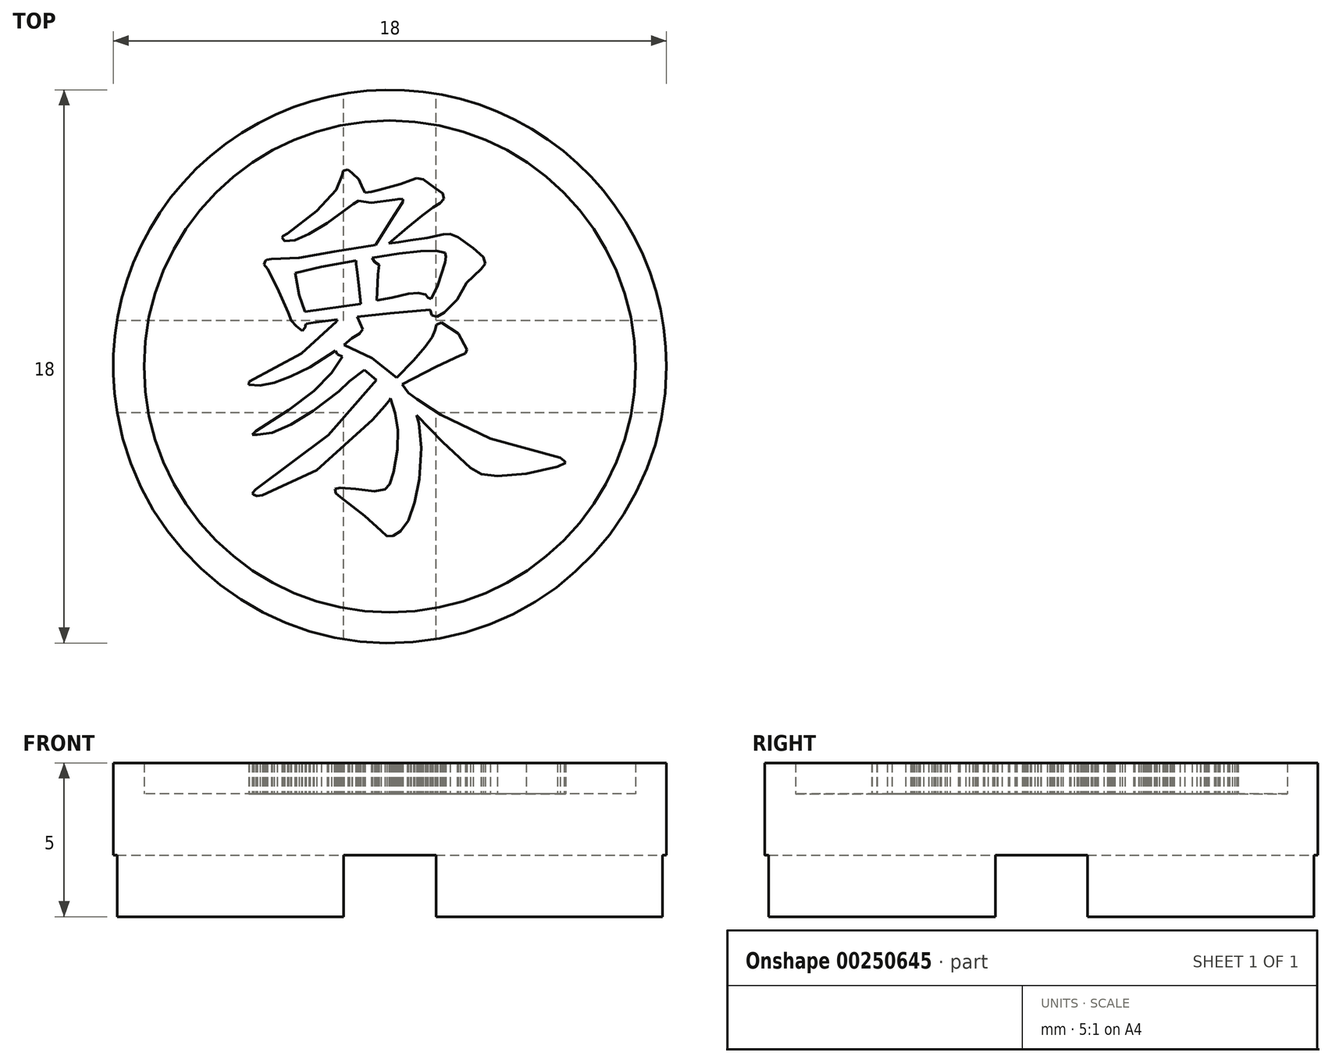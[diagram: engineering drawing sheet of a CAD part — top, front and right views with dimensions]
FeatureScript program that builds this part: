
annotation { "Feature Type Name" : "Feature", "Feature Type Description" : "" }
export const myFeature = defineFeature(function(context is Context, id is Id, definition is map)
    precondition{}
    {
        {
            var Q0;
            Q0=qCreatedBy(makeId("Top.planeOp"),FACE);
            var sketch = newSketch(context, id + "F0", { "sketchPlane" : qUnion([Q0])});
            skCircle(sketch, "E0", {"center": v(-31.33, 19.76) * mm, "radius": 9 * mm});
            skSolve(sketch);
        }
        {
            var Q0;
            Q0=qSketchRegion(id+"F0",true);
            extrude(context, id + "F1", {"entities" : qUnion([Q0]), "depth" : 4 * mm});
        }
        {
            var Q0;
            Q0=makeQuery(id+"F1.opExtrude","CAP_FACE",FACE,{"disambiguationData":[OSD([sQuery(id+"F0.wireOp",EDGE,"E0")])],"isStart":false});
            var sketch = newSketch(context, id + "F2", { "sketchPlane" : qUnion([Q0])});
            skCircle(sketch, "E1", {"center": v(-31.33, 19.76) * mm, "radius": 8 * mm});
            skCircle(sketch, "E2", {"center": v(-31.33, 19.76) * mm, "radius": 9 * mm});
            skSolve(sketch);
        }
        {
            var Q0;
            Q0=makeQuery(id+"F1.opExtrude","CAP_FACE",FACE,{"disambiguationData":[OSD([sQuery(id+"F0.wireOp",EDGE,"E0")])],"isStart":true});
            var sketch = newSketch(context, id + "F3", { "sketchPlane" : qUnion([Q0])});
            skLineSegment(sketch, "E3", {"start": v(-31.33, -19.76) * mm, "end": v(-22.33, -19.76) * mm, "construction": true});
            skLineSegment(sketch, "E4", {"start": v(-31.33, -19.76) * mm, "end": v(-31.33, -10.76) * mm, "construction": true});
            skLineSegment(sketch, "E5", {"start": v(-31.33, -19.76) * mm, "end": v(-40.33, -19.76) * mm, "construction": true});
            skLineSegment(sketch, "E6", {"start": v(-31.33, -19.76) * mm, "end": v(-31.33, -28.76) * mm, "construction": true});
            skLineSegment(sketch, "E7.bottom", {"start": v(-40.33, -28.76) * mm, "end": v(-22.33, -28.76) * mm});
            skLineSegment(sketch, "E7.top", {"start": v(-40.33, -10.76) * mm, "end": v(-22.33, -10.76) * mm});
            skLineSegment(sketch, "E7.left", {"start": v(-22.33, -10.76) * mm, "end": v(-22.33, -28.76) * mm});
            skLineSegment(sketch, "E7.right", {"start": v(-40.33, -10.76) * mm, "end": v(-40.33, -28.76) * mm});
            skPoint(sketch, "E8", {"position": v(-31.33, -28.76) * mm});
            skPoint(sketch, "E9", {"position": v(-40.33, -19.76) * mm});
            skPoint(sketch, "E10", {"position": v(-22.33, -19.76) * mm});
            skPoint(sketch, "E11", {"position": v(-31.33, -10.76) * mm});
            skLineSegment(sketch, "E12.bottom", {"start": v(-32.83, -10.76) * mm, "end": v(-29.83, -10.76) * mm});
            skLineSegment(sketch, "E12.top", {"start": v(-32.83, -28.76) * mm, "end": v(-29.83, -28.76) * mm});
            skLineSegment(sketch, "E12.left", {"start": v(-32.83, -10.76) * mm, "end": v(-32.83, -28.76) * mm});
            skLineSegment(sketch, "E12.right", {"start": v(-29.83, -10.76) * mm, "end": v(-29.83, -28.76) * mm});
            skLineSegment(sketch, "E13.bottom", {"start": v(-40.33, -18.26) * mm, "end": v(-22.33, -18.26) * mm});
            skLineSegment(sketch, "E13.top", {"start": v(-40.33, -21.26) * mm, "end": v(-22.33, -21.26) * mm});
            skLineSegment(sketch, "E13.left", {"start": v(-40.33, -18.26) * mm, "end": v(-40.33, -21.26) * mm});
            skLineSegment(sketch, "E13.right", {"start": v(-22.33, -18.26) * mm, "end": v(-22.33, -21.26) * mm});
            skSolve(sketch);
        }
        {
            var Q0;
            {var subQ1=sQuery(id+"F3.wireOp",EDGE,"E12.bottom");var subQ3=makeQuery(id+"F1.opExtrude","CAP_EDGE",EDGE,{"disambiguationData":[OSD([sQuery(id+"F0.wireOp",EDGE,"E0")])],"isStart":true});var subQ4=makeQuery(id+"F3.imprint","INTERSECT",VERTEX,{"derivedFrom":[subQ3,subQ1]});Q0=makeQuery(id+"F3.imprint","IMPRINT",FACE,{"disambiguationData":[TD([[makeQuery(id+"F3.imprint","IMPRINT",EDGE,{"disambiguationData":[TD([[subQ4,1.0]])],"derivedFrom":subQ3}),1.0]])]});}
            var Q1;
            {var subQ1=sQuery(id+"F3.wireOp",EDGE,"E12.bottom");var subQ3=makeQuery(id+"F1.opExtrude","CAP_EDGE",EDGE,{"disambiguationData":[OSD([sQuery(id+"F0.wireOp",EDGE,"E0")])],"isStart":true});var subQ4=makeQuery(id+"F3.imprint","INTERSECT",VERTEX,{"derivedFrom":[subQ3,subQ1]});Q1=makeQuery(id+"F3.imprint","IMPRINT",FACE,{"disambiguationData":[TD([[makeQuery(id+"F3.imprint","IMPRINT",EDGE,{"disambiguationData":[TD([[subQ4,-1.0]])],"derivedFrom":subQ3}),1.0]])]});}
            var Q2;
            {var subQ1=sQuery(id+"F3.wireOp",EDGE,"E12.top");var subQ3=makeQuery(id+"F1.opExtrude","CAP_EDGE",EDGE,{"disambiguationData":[OSD([sQuery(id+"F0.wireOp",EDGE,"E0")])],"isStart":true});var subQ4=makeQuery(id+"F3.imprint","INTERSECT",VERTEX,{"derivedFrom":[subQ3,subQ1]});Q2=makeQuery(id+"F3.imprint","IMPRINT",FACE,{"disambiguationData":[TD([[makeQuery(id+"F3.imprint","IMPRINT",EDGE,{"disambiguationData":[TD([[subQ4,-1.0]])],"derivedFrom":subQ3}),1.0]])]});}
            var Q3;
            {var subQ1=sQuery(id+"F3.wireOp",EDGE,"E12.top");var subQ3=makeQuery(id+"F1.opExtrude","CAP_EDGE",EDGE,{"disambiguationData":[OSD([sQuery(id+"F0.wireOp",EDGE,"E0")])],"isStart":true});var subQ4=makeQuery(id+"F3.imprint","INTERSECT",VERTEX,{"derivedFrom":[subQ3,subQ1]});Q3=makeQuery(id+"F3.imprint","IMPRINT",FACE,{"disambiguationData":[TD([[makeQuery(id+"F3.imprint","IMPRINT",EDGE,{"disambiguationData":[TD([[subQ4,1.0]])],"derivedFrom":subQ3}),1.0]])]});}
            var Q4;
            {var subQ0=sQuery(id+"F3.wireOp",EDGE,"E13.left");var subQ3=makeQuery(id+"F1.opExtrude","CAP_EDGE",EDGE,{"disambiguationData":[OSD([sQuery(id+"F0.wireOp",EDGE,"E0")])],"isStart":true});var subQ5=makeQuery(id+"F3.imprint","INTERSECT",VERTEX,{"derivedFrom":[subQ3,subQ0]});Q4=makeQuery(id+"F3.imprint","IMPRINT",FACE,{"disambiguationData":[TD([[makeQuery(id+"F3.imprint","IMPRINT",EDGE,{"disambiguationData":[TD([[subQ5,-1.0]])],"derivedFrom":subQ3}),1.0]])]});}
            var Q5;
            {var subQ0=sQuery(id+"F3.wireOp",EDGE,"E13.right");var subQ3=makeQuery(id+"F1.opExtrude","CAP_EDGE",EDGE,{"disambiguationData":[OSD([sQuery(id+"F0.wireOp",EDGE,"E0")])],"isStart":true});var subQ5=makeQuery(id+"F3.imprint","INTERSECT",VERTEX,{"derivedFrom":[subQ3,subQ0]});Q5=makeQuery(id+"F3.imprint","IMPRINT",FACE,{"disambiguationData":[TD([[makeQuery(id+"F3.imprint","IMPRINT",EDGE,{"disambiguationData":[TD([[subQ5,1.0]])],"derivedFrom":subQ3}),1.0]])]});}
            var Q6;
            {var subQ0=sQuery(id+"F3.wireOp",EDGE,"E13.left");var subQ3=makeQuery(id+"F1.opExtrude","CAP_EDGE",EDGE,{"disambiguationData":[OSD([sQuery(id+"F0.wireOp",EDGE,"E0")])],"isStart":true});var subQ5=makeQuery(id+"F3.imprint","INTERSECT",VERTEX,{"derivedFrom":[subQ3,subQ0]});Q6=makeQuery(id+"F3.imprint","IMPRINT",FACE,{"disambiguationData":[TD([[makeQuery(id+"F3.imprint","IMPRINT",EDGE,{"disambiguationData":[TD([[subQ5,1.0]])],"derivedFrom":subQ3}),1.0]])]});}
            var Q7;
            {var subQ0=sQuery(id+"F3.wireOp",EDGE,"E13.right");var subQ3=makeQuery(id+"F1.opExtrude","CAP_EDGE",EDGE,{"disambiguationData":[OSD([sQuery(id+"F0.wireOp",EDGE,"E0")])],"isStart":true});var subQ5=makeQuery(id+"F3.imprint","INTERSECT",VERTEX,{"derivedFrom":[subQ3,subQ0]});Q7=makeQuery(id+"F3.imprint","IMPRINT",FACE,{"disambiguationData":[TD([[makeQuery(id+"F3.imprint","IMPRINT",EDGE,{"disambiguationData":[TD([[subQ5,-1.0]])],"derivedFrom":subQ3}),1.0]])]});}
            var Q8;
            {var subQ3=makeQuery(id+"F1.opExtrude","CAP_EDGE",EDGE,{"disambiguationData":[OSD([sQuery(id+"F0.wireOp",EDGE,"E0")])],"isStart":true});var subQ5=sQuery(id+"F3.wireOp",EDGE,"E12.left");var subQ8=makeQuery(id+"F3.imprint","INTERSECT",VERTEX,{"disambiguationData":[OD(1.0)],"derivedFrom":[subQ3,subQ5]});Q8=makeQuery(id+"F3.imprint","IMPRINT",FACE,{"disambiguationData":[TD([[makeQuery(id+"F3.imprint","IMPRINT",EDGE,{"disambiguationData":[TD([[subQ8,-1.0]])],"derivedFrom":subQ3}),1.0]])]});}
            var Q9;
            {var subQ3=makeQuery(id+"F1.opExtrude","CAP_EDGE",EDGE,{"disambiguationData":[OSD([sQuery(id+"F0.wireOp",EDGE,"E0")])],"isStart":true});var subQ5=sQuery(id+"F3.wireOp",EDGE,"E12.right");var subQ8=makeQuery(id+"F3.imprint","INTERSECT",VERTEX,{"disambiguationData":[OD(1.0)],"derivedFrom":[subQ3,subQ5]});Q9=makeQuery(id+"F3.imprint","IMPRINT",FACE,{"disambiguationData":[TD([[makeQuery(id+"F3.imprint","IMPRINT",EDGE,{"disambiguationData":[TD([[subQ8,1.0]])],"derivedFrom":subQ3}),1.0]])]});}
            var Q10;
            {var subQ3=makeQuery(id+"F1.opExtrude","CAP_EDGE",EDGE,{"disambiguationData":[OSD([sQuery(id+"F0.wireOp",EDGE,"E0")])],"isStart":true});var subQ5=sQuery(id+"F3.wireOp",EDGE,"E12.left");var subQ8=makeQuery(id+"F3.imprint","INTERSECT",VERTEX,{"disambiguationData":[OD(0.0)],"derivedFrom":[subQ3,subQ5]});Q10=makeQuery(id+"F3.imprint","IMPRINT",FACE,{"disambiguationData":[TD([[makeQuery(id+"F3.imprint","IMPRINT",EDGE,{"disambiguationData":[TD([[subQ8,1.0]])],"derivedFrom":subQ3}),1.0]])]});}
            var Q11;
            {var subQ3=makeQuery(id+"F1.opExtrude","CAP_EDGE",EDGE,{"disambiguationData":[OSD([sQuery(id+"F0.wireOp",EDGE,"E0")])],"isStart":true});var subQ5=sQuery(id+"F3.wireOp",EDGE,"E12.right");var subQ8=makeQuery(id+"F3.imprint","INTERSECT",VERTEX,{"disambiguationData":[OD(0.0)],"derivedFrom":[subQ3,subQ5]});Q11=makeQuery(id+"F3.imprint","IMPRINT",FACE,{"disambiguationData":[TD([[makeQuery(id+"F3.imprint","IMPRINT",EDGE,{"disambiguationData":[TD([[subQ8,-1.0]])],"derivedFrom":subQ3}),1.0]])]});}
            var Q12;
            {var subQ2=sQuery(id+"F3.wireOp",EDGE,"E12.left");var subQ4=sQuery(id+"F3.wireOp",EDGE,"E13.bottom");var subQ8=makeQuery(id+"F3.imprint","INTERSECT",VERTEX,{"derivedFrom":[subQ2,subQ4]});Q12=makeQuery(id+"F3.imprint","IMPRINT",FACE,{"disambiguationData":[TD([[makeQuery(id+"F3.imprint","IMPRINT",EDGE,{"disambiguationData":[TD([[subQ8,1.0]])],"derivedFrom":subQ2}),1.0]])]});}
            var Q13;
            {var subQ1=sQuery(id+"F3.wireOp",EDGE,"E12.left");var subQ5=sQuery(id+"F3.wireOp",EDGE,"E13.bottom");var subQ6=makeQuery(id+"F3.imprint","INTERSECT",VERTEX,{"derivedFrom":[subQ1,subQ5]});Q13=makeQuery(id+"F3.imprint","IMPRINT",FACE,{"disambiguationData":[TD([[makeQuery(id+"F3.imprint","IMPRINT",EDGE,{"disambiguationData":[TD([[subQ6,-1.0]])],"derivedFrom":subQ1}),-1.0]])]});}
            var Q14;
            {var subQ0=sQuery(id+"F3.wireOp",EDGE,"E13.top");var subQ1=sQuery(id+"F3.wireOp",EDGE,"E12.left");var subQ2=makeQuery(id+"F3.imprint","INTERSECT",VERTEX,{"derivedFrom":[subQ1,subQ0]});Q14=makeQuery(id+"F3.imprint","IMPRINT",FACE,{"disambiguationData":[TD([[makeQuery(id+"F3.imprint","IMPRINT",EDGE,{"disambiguationData":[TD([[subQ2,-1.0]])],"derivedFrom":subQ1}),1.0]])]});}
            var Q15;
            {var subQ2=sQuery(id+"F3.wireOp",EDGE,"E13.bottom");var subQ5=sQuery(id+"F3.wireOp",EDGE,"E12.right");var subQ8=makeQuery(id+"F3.imprint","INTERSECT",VERTEX,{"derivedFrom":[subQ5,subQ2]});Q15=makeQuery(id+"F3.imprint","IMPRINT",FACE,{"disambiguationData":[TD([[makeQuery(id+"F3.imprint","IMPRINT",EDGE,{"disambiguationData":[TD([[subQ8,-1.0]])],"derivedFrom":subQ5}),1.0]])]});}
            var Q16;
            {var subQ0=sQuery(id+"F3.wireOp",EDGE,"E13.bottom");var subQ1=sQuery(id+"F3.wireOp",EDGE,"E12.left");var subQ2=makeQuery(id+"F3.imprint","INTERSECT",VERTEX,{"derivedFrom":[subQ1,subQ0]});Q16=makeQuery(id+"F3.imprint","IMPRINT",FACE,{"disambiguationData":[TD([[makeQuery(id+"F3.imprint","IMPRINT",EDGE,{"disambiguationData":[TD([[subQ2,-1.0]])],"derivedFrom":subQ1}),1.0]])]});}
            extrude(context, id + "F4", {"entities" : qUnion([Q0, Q1, Q2, Q3, Q4, Q5, Q6, Q7, Q8, Q9, Q10, Q11, Q12, Q13, Q14, Q15, Q16]), "operationType" : NewBodyOperationType.REMOVE, "oppositeDirection" : true, "depth" : 2 * mm});
        }
        {
            var Q0;
            Q0=qSketchRegion(id+"F2",true);
            var Q1;
            Q1=makeQuery(id+"F2.imprint","IMPRINT",FACE,{"disambiguationData":[TD([[makeQuery(id+"F2.imprint","IMPRINT",EDGE,{"derivedFrom":sQuery(id+"F2.wireOp",EDGE,"hKqnuJLd-dfdz-vJIs-yDKo-c4hLNRw30SuP")}),-1.0]])]});
            extrude(context, id + "F5", {"entities" : qUnion([Q0, Q1]), "operationType" : NewBodyOperationType.ADD, "depth" : 1 * mm});
        }
        {
            var Q0;
            Q0=makeQuery(id+"F1.opExtrude","CAP_FACE",FACE,{"disambiguationData":[OSD([sQuery(id+"F0.wireOp",EDGE,"E0")])],"isStart":false});
            var sketch = newSketch(context, id + "F6", { "sketchPlane" : qUnion([Q0])});
            skLineSegment(sketch, "E14", {"start": v(-30.46, 18.17) * mm, "end": v(-29.61, 17.3) * mm});
            skLineSegment(sketch, "E15", {"start": v(-29.61, 17.3) * mm, "end": v(-28.7, 16.46) * mm});
            skLineSegment(sketch, "E16", {"start": v(-28.7, 16.46) * mm, "end": v(-28.35, 16.25) * mm});
            skLineSegment(sketch, "E17", {"start": v(-28.35, 16.25) * mm, "end": v(-27.84, 16.2) * mm});
            skLineSegment(sketch, "E18", {"start": v(-27.84, 16.2) * mm, "end": v(-26.89, 16.27) * mm});
            skLineSegment(sketch, "E19", {"start": v(-26.89, 16.27) * mm, "end": v(-25.88, 16.5) * mm});
            skLineSegment(sketch, "E20", {"start": v(-25.88, 16.5) * mm, "end": v(-25.6, 16.62) * mm});
            skLineSegment(sketch, "E21", {"start": v(-25.6, 16.62) * mm, "end": v(-25.66, 16.69) * mm});
            skLineSegment(sketch, "E22", {"start": v(-25.66, 16.69) * mm, "end": v(-25.8, 16.79) * mm});
            skLineSegment(sketch, "E23", {"start": v(-25.8, 16.79) * mm, "end": v(-28.06, 17.41) * mm});
            skLineSegment(sketch, "E24", {"start": v(-28.06, 17.41) * mm, "end": v(-29.67, 18.19) * mm});
            skLineSegment(sketch, "E25", {"start": v(-29.67, 18.19) * mm, "end": v(-29.97, 18.38) * mm});
            skLineSegment(sketch, "E26", {"start": v(-29.97, 18.38) * mm, "end": v(-30.44, 18.7) * mm});
            skLineSegment(sketch, "E27", {"start": v(-30.44, 18.7) * mm, "end": v(-30.73, 18.9) * mm});
            skLineSegment(sketch, "E28", {"start": v(-30.73, 18.9) * mm, "end": v(-30.93, 19.18) * mm});
            skLineSegment(sketch, "E29", {"start": v(-30.93, 19.18) * mm, "end": v(-29.83, 19.74) * mm});
            skLineSegment(sketch, "E30", {"start": v(-29.83, 19.74) * mm, "end": v(-29.04, 20.12) * mm});
            skLineSegment(sketch, "E31", {"start": v(-29.04, 20.12) * mm, "end": v(-28.87, 20.18) * mm});
            skLineSegment(sketch, "E32", {"start": v(-28.87, 20.18) * mm, "end": v(-28.82, 20.3) * mm});
            skLineSegment(sketch, "E33", {"start": v(-28.82, 20.3) * mm, "end": v(-29.1, 20.83) * mm});
            skLineSegment(sketch, "E34", {"start": v(-29.1, 20.83) * mm, "end": v(-29.65, 21.18) * mm});
            skLineSegment(sketch, "E35", {"start": v(-29.65, 21.18) * mm, "end": v(-29.82, 21.12) * mm});
            skLineSegment(sketch, "E36", {"start": v(-29.82, 21.12) * mm, "end": v(-29.87, 20.93) * mm});
            skLineSegment(sketch, "E37", {"start": v(-29.87, 20.93) * mm, "end": v(-29.95, 20.72) * mm});
            skLineSegment(sketch, "E38", {"start": v(-29.95, 20.72) * mm, "end": v(-30.18, 20.4) * mm});
            skLineSegment(sketch, "E39", {"start": v(-30.18, 20.4) * mm, "end": v(-30.56, 19.95) * mm});
            skLineSegment(sketch, "E40", {"start": v(-30.56, 19.95) * mm, "end": v(-31.1, 19.4) * mm});
            skLineSegment(sketch, "E41", {"start": v(-31.1, 19.4) * mm, "end": v(-31.9, 20.04) * mm});
            skLineSegment(sketch, "E42", {"start": v(-31.9, 20.04) * mm, "end": v(-32.82, 20.47) * mm});
            skLineSegment(sketch, "E43", {"start": v(-32.82, 20.47) * mm, "end": v(-32.57, 20.68) * mm});
            skLineSegment(sketch, "E44", {"start": v(-32.57, 20.68) * mm, "end": v(-32.31, 20.83) * mm});
            skLineSegment(sketch, "E45", {"start": v(-32.31, 20.83) * mm, "end": v(-32.2, 20.97) * mm});
            skLineSegment(sketch, "E46", {"start": v(-32.2, 20.97) * mm, "end": v(-32.39, 21.37) * mm});
            skLineSegment(sketch, "E47", {"start": v(-32.39, 21.37) * mm, "end": v(-31.33, 21.5) * mm});
            skLineSegment(sketch, "E48", {"start": v(-31.33, 21.5) * mm, "end": v(-30.02, 21.6) * mm});
            skLineSegment(sketch, "E49", {"start": v(-30.02, 21.6) * mm, "end": v(-30.01, 21.6) * mm});
            skLineSegment(sketch, "E50", {"start": v(-30.01, 21.6) * mm, "end": v(-29.96, 21.43) * mm});
            skLineSegment(sketch, "E51", {"start": v(-29.96, 21.43) * mm, "end": v(-29.8, 21.37) * mm});
            skLineSegment(sketch, "E52", {"start": v(-29.8, 21.37) * mm, "end": v(-29.55, 21.52) * mm});
            skLineSegment(sketch, "E53", {"start": v(-29.55, 21.52) * mm, "end": v(-29.14, 21.93) * mm});
            skLineSegment(sketch, "E54", {"start": v(-29.14, 21.93) * mm, "end": v(-28.84, 22.48) * mm});
            skLineSegment(sketch, "E55", {"start": v(-28.84, 22.48) * mm, "end": v(-28.37, 22.93) * mm});
            skLineSegment(sketch, "E56", {"start": v(-28.37, 22.93) * mm, "end": v(-28.22, 23.1) * mm});
            skLineSegment(sketch, "E57", {"start": v(-28.22, 23.1) * mm, "end": v(-28.3, 23.32) * mm});
            skLineSegment(sketch, "E58", {"start": v(-28.3, 23.32) * mm, "end": v(-28.62, 23.6) * mm});
            skLineSegment(sketch, "E59", {"start": v(-28.62, 23.6) * mm, "end": v(-29.12, 23.97) * mm});
            skLineSegment(sketch, "E60", {"start": v(-29.12, 23.97) * mm, "end": v(-29.37, 24.06) * mm});
            skLineSegment(sketch, "E61", {"start": v(-29.37, 24.06) * mm, "end": v(-29.6, 24.05) * mm});
            skLineSegment(sketch, "E62", {"start": v(-29.6, 24.05) * mm, "end": v(-30.12, 23.94) * mm});
            skLineSegment(sketch, "E63", {"start": v(-30.12, 23.94) * mm, "end": v(-30.67, 23.87) * mm});
            skLineSegment(sketch, "E64", {"start": v(-30.67, 23.87) * mm, "end": v(-31.04, 23.8) * mm});
            skLineSegment(sketch, "E65", {"start": v(-31.04, 23.8) * mm, "end": v(-31.37, 23.76) * mm});
            skLineSegment(sketch, "E66", {"start": v(-31.37, 23.76) * mm, "end": v(-30.77, 24.28) * mm});
            skLineSegment(sketch, "E67", {"start": v(-30.77, 24.28) * mm, "end": v(-30.28, 24.67) * mm});
            skLineSegment(sketch, "E68", {"start": v(-30.28, 24.67) * mm, "end": v(-29.93, 24.94) * mm});
            skLineSegment(sketch, "E69", {"start": v(-29.93, 24.94) * mm, "end": v(-29.7, 25.07) * mm});
            skLineSegment(sketch, "E70", {"start": v(-29.7, 25.07) * mm, "end": v(-29.57, 25.2) * mm});
            skLineSegment(sketch, "E71", {"start": v(-29.57, 25.2) * mm, "end": v(-29.6, 25.38) * mm});
            skLineSegment(sketch, "E72", {"start": v(-29.6, 25.38) * mm, "end": v(-29.87, 25.56) * mm});
            skLineSegment(sketch, "E73", {"start": v(-29.87, 25.56) * mm, "end": v(-30.24, 25.85) * mm});
            skLineSegment(sketch, "E74", {"start": v(-30.24, 25.85) * mm, "end": v(-30.46, 25.89) * mm});
            skLineSegment(sketch, "E75", {"start": v(-30.46, 25.89) * mm, "end": v(-30.64, 25.82) * mm});
            skLineSegment(sketch, "E76", {"start": v(-30.64, 25.82) * mm, "end": v(-30.98, 25.7) * mm});
            skLineSegment(sketch, "E77", {"start": v(-30.98, 25.7) * mm, "end": v(-31.68, 25.5) * mm});
            skLineSegment(sketch, "E78", {"start": v(-31.68, 25.5) * mm, "end": v(-31.94, 25.44) * mm});
            skLineSegment(sketch, "E79", {"start": v(-31.94, 25.44) * mm, "end": v(-32.14, 25.4) * mm});
            skLineSegment(sketch, "E80", {"start": v(-32.14, 25.4) * mm, "end": v(-32.21, 25.56) * mm});
            skLineSegment(sketch, "E81", {"start": v(-32.21, 25.56) * mm, "end": v(-32.34, 25.85) * mm});
            skLineSegment(sketch, "E82", {"start": v(-32.34, 25.85) * mm, "end": v(-32.55, 26.05) * mm});
            skLineSegment(sketch, "E83", {"start": v(-32.55, 26.05) * mm, "end": v(-32.7, 26.16) * mm});
            skLineSegment(sketch, "E84", {"start": v(-32.7, 26.16) * mm, "end": v(-32.85, 26.12) * mm});
            skLineSegment(sketch, "E85", {"start": v(-32.85, 26.12) * mm, "end": v(-32.88, 25.97) * mm});
            skLineSegment(sketch, "E86", {"start": v(-32.88, 25.97) * mm, "end": v(-33.07, 25.5) * mm});
            skLineSegment(sketch, "E87", {"start": v(-33.07, 25.5) * mm, "end": v(-33.7, 24.81) * mm});
            skLineSegment(sketch, "E88", {"start": v(-33.7, 24.81) * mm, "end": v(-34.67, 24.08) * mm});
            skLineSegment(sketch, "E89", {"start": v(-34.67, 24.08) * mm, "end": v(-34.8, 24) * mm});
            skLineSegment(sketch, "E90", {"start": v(-34.8, 24) * mm, "end": v(-34.84, 23.96) * mm});
            skLineSegment(sketch, "E91", {"start": v(-34.84, 23.96) * mm, "end": v(-34.76, 23.84) * mm});
            skLineSegment(sketch, "E92", {"start": v(-34.76, 23.84) * mm, "end": v(-34.43, 23.86) * mm});
            skLineSegment(sketch, "E93", {"start": v(-34.43, 23.86) * mm, "end": v(-33.96, 24.06) * mm});
            skLineSegment(sketch, "E94", {"start": v(-33.96, 24.06) * mm, "end": v(-33.37, 24.43) * mm});
            skLineSegment(sketch, "E95", {"start": v(-33.37, 24.43) * mm, "end": v(-32.66, 24.94) * mm});
            skLineSegment(sketch, "E96", {"start": v(-32.66, 24.94) * mm, "end": v(-32.52, 25.04) * mm});
            skLineSegment(sketch, "E97", {"start": v(-32.52, 25.04) * mm, "end": v(-32.35, 25.15) * mm});
            skLineSegment(sketch, "E98", {"start": v(-32.35, 25.15) * mm, "end": v(-31.94, 25.08) * mm});
            skLineSegment(sketch, "E99", {"start": v(-31.94, 25.08) * mm, "end": v(-31.16, 25.19) * mm});
            skLineSegment(sketch, "E100", {"start": v(-31.16, 25.19) * mm, "end": v(-31, 25.2) * mm});
            skLineSegment(sketch, "E101", {"start": v(-31, 25.2) * mm, "end": v(-30.9, 25.2) * mm});
            skLineSegment(sketch, "E102", {"start": v(-30.9, 25.2) * mm, "end": v(-30.9, 25.12) * mm});
            skLineSegment(sketch, "E103", {"start": v(-30.9, 25.12) * mm, "end": v(-30.94, 25.06) * mm});
            skLineSegment(sketch, "E104", {"start": v(-30.94, 25.06) * mm, "end": v(-31.28, 24.52) * mm});
            skLineSegment(sketch, "E105", {"start": v(-31.28, 24.52) * mm, "end": v(-31.8, 23.71) * mm});
            skLineSegment(sketch, "E106", {"start": v(-31.8, 23.71) * mm, "end": v(-33.14, 23.5) * mm});
            skLineSegment(sketch, "E107", {"start": v(-33.14, 23.5) * mm, "end": v(-34.28, 23.3) * mm});
            skLineSegment(sketch, "E108", {"start": v(-34.28, 23.3) * mm, "end": v(-35.19, 23.26) * mm});
            skLineSegment(sketch, "E109", {"start": v(-35.19, 23.26) * mm, "end": v(-35.33, 23.23) * mm});
            skLineSegment(sketch, "E110", {"start": v(-35.33, 23.23) * mm, "end": v(-35.38, 23.2) * mm});
            skLineSegment(sketch, "E111", {"start": v(-35.38, 23.2) * mm, "end": v(-35.42, 23.08) * mm});
            skLineSegment(sketch, "E112", {"start": v(-35.42, 23.08) * mm, "end": v(-35.32, 22.94) * mm});
            skLineSegment(sketch, "E113", {"start": v(-35.32, 22.94) * mm, "end": v(-35, 22.31) * mm});
            skLineSegment(sketch, "E114", {"start": v(-35, 22.31) * mm, "end": v(-34.64, 21.52) * mm});
            skLineSegment(sketch, "E115", {"start": v(-34.64, 21.52) * mm, "end": v(-34.54, 21.25) * mm});
            skLineSegment(sketch, "E116", {"start": v(-34.54, 21.25) * mm, "end": v(-34.37, 21.08) * mm});
            skLineSegment(sketch, "E117", {"start": v(-34.37, 21.08) * mm, "end": v(-34.18, 20.92) * mm});
            skLineSegment(sketch, "E118", {"start": v(-34.18, 20.92) * mm, "end": v(-34.07, 21.03) * mm});
            skLineSegment(sketch, "E119", {"start": v(-34.07, 21.03) * mm, "end": v(-34.08, 21.08) * mm});
            skLineSegment(sketch, "E120", {"start": v(-34.08, 21.08) * mm, "end": v(-34.06, 21.15) * mm});
            skLineSegment(sketch, "E121", {"start": v(-34.06, 21.15) * mm, "end": v(-33.82, 21.18) * mm});
            skLineSegment(sketch, "E122", {"start": v(-33.82, 21.18) * mm, "end": v(-33.04, 21.28) * mm});
            skLineSegment(sketch, "E123", {"start": v(-33.04, 21.28) * mm, "end": v(-33.07, 21.24) * mm});
            skLineSegment(sketch, "E124", {"start": v(-33.07, 21.24) * mm, "end": v(-33.06, 21.22) * mm});
            skLineSegment(sketch, "E125", {"start": v(-33.06, 21.22) * mm, "end": v(-34.2, 20.18) * mm});
            skLineSegment(sketch, "E126", {"start": v(-34.2, 20.18) * mm, "end": v(-35.91, 19.26) * mm});
            skLineSegment(sketch, "E127", {"start": v(-35.91, 19.26) * mm, "end": v(-35.93, 19.17) * mm});
            skLineSegment(sketch, "E128", {"start": v(-35.93, 19.17) * mm, "end": v(-35.56, 19.14) * mm});
            skLineSegment(sketch, "E129", {"start": v(-35.56, 19.14) * mm, "end": v(-35.1, 19.23) * mm});
            skLineSegment(sketch, "E130", {"start": v(-35.1, 19.23) * mm, "end": v(-34.56, 19.44) * mm});
            skLineSegment(sketch, "E131", {"start": v(-34.56, 19.44) * mm, "end": v(-33.93, 19.74) * mm});
            skLineSegment(sketch, "E132", {"start": v(-33.93, 19.74) * mm, "end": v(-33.72, 19.88) * mm});
            skLineSegment(sketch, "E133", {"start": v(-33.72, 19.88) * mm, "end": v(-33.1, 20.27) * mm});
            skLineSegment(sketch, "E134", {"start": v(-33.1, 20.27) * mm, "end": v(-33.03, 20.16) * mm});
            skLineSegment(sketch, "E135", {"start": v(-33.03, 20.16) * mm, "end": v(-32.87, 20.08) * mm});
            skLineSegment(sketch, "E136", {"start": v(-32.87, 20.08) * mm, "end": v(-33.22, 19.55) * mm});
            skLineSegment(sketch, "E137", {"start": v(-33.22, 19.55) * mm, "end": v(-33.8, 18.97) * mm});
            skLineSegment(sketch, "E138", {"start": v(-33.8, 18.97) * mm, "end": v(-34.63, 18.34) * mm});
            skLineSegment(sketch, "E139", {"start": v(-34.63, 18.34) * mm, "end": v(-35.7, 17.66) * mm});
            skLineSegment(sketch, "E140", {"start": v(-35.7, 17.66) * mm, "end": v(-35.8, 17.54) * mm});
            skLineSegment(sketch, "E141", {"start": v(-35.8, 17.54) * mm, "end": v(-35.64, 17.54) * mm});
            skLineSegment(sketch, "E142", {"start": v(-35.64, 17.54) * mm, "end": v(-35.16, 17.6) * mm});
            skLineSegment(sketch, "E143", {"start": v(-35.16, 17.6) * mm, "end": v(-34.56, 17.87) * mm});
            skLineSegment(sketch, "E144", {"start": v(-34.56, 17.87) * mm, "end": v(-33.83, 18.32) * mm});
            skLineSegment(sketch, "E145", {"start": v(-33.83, 18.32) * mm, "end": v(-32.98, 18.95) * mm});
            skLineSegment(sketch, "E146", {"start": v(-32.98, 18.95) * mm, "end": v(-32.64, 19.28) * mm});
            skLineSegment(sketch, "E147", {"start": v(-32.64, 19.28) * mm, "end": v(-32.17, 19.64) * mm});
            skLineSegment(sketch, "E148", {"start": v(-32.17, 19.64) * mm, "end": v(-32.18, 19.62) * mm});
            skLineSegment(sketch, "E149", {"start": v(-32.18, 19.62) * mm, "end": v(-32.16, 19.65) * mm});
            skLineSegment(sketch, "E150", {"start": v(-32.16, 19.65) * mm, "end": v(-31.77, 19.31) * mm});
            skLineSegment(sketch, "E151", {"start": v(-31.77, 19.31) * mm, "end": v(-33.33, 17.52) * mm});
            skLineSegment(sketch, "E152", {"start": v(-33.33, 17.52) * mm, "end": v(-35.7, 15.77) * mm});
            skLineSegment(sketch, "E153", {"start": v(-35.7, 15.77) * mm, "end": v(-35.8, 15.63) * mm});
            skLineSegment(sketch, "E154", {"start": v(-35.8, 15.63) * mm, "end": v(-35.75, 15.59) * mm});
            skLineSegment(sketch, "E155", {"start": v(-35.75, 15.59) * mm, "end": v(-35.65, 15.54) * mm});
            skLineSegment(sketch, "E156", {"start": v(-35.65, 15.54) * mm, "end": v(-35.47, 15.57) * mm});
            skLineSegment(sketch, "E157", {"start": v(-35.47, 15.57) * mm, "end": v(-33.71, 16.38) * mm});
            skLineSegment(sketch, "E158", {"start": v(-33.71, 16.38) * mm, "end": v(-31.9, 18.02) * mm});
            skLineSegment(sketch, "E159", {"start": v(-31.9, 18.02) * mm, "end": v(-31.49, 18.48) * mm});
            skLineSegment(sketch, "E160", {"start": v(-31.49, 18.48) * mm, "end": v(-31.33, 18.68) * mm});
            skLineSegment(sketch, "E161", {"start": v(-31.33, 18.68) * mm, "end": v(-31.33, 18.68) * mm});
            skLineSegment(sketch, "E162", {"start": v(-31.33, 18.68) * mm, "end": v(-31.31, 18.72) * mm});
            skLineSegment(sketch, "E163", {"start": v(-31.31, 18.72) * mm, "end": v(-31.15, 18.24) * mm});
            skLineSegment(sketch, "E164", {"start": v(-31.15, 18.24) * mm, "end": v(-31.07, 17.7) * mm});
            skLineSegment(sketch, "E165", {"start": v(-31.07, 17.7) * mm, "end": v(-31.09, 17.06) * mm});
            skLineSegment(sketch, "E166", {"start": v(-31.09, 17.06) * mm, "end": v(-31.21, 16.32) * mm});
            skLineSegment(sketch, "E167", {"start": v(-31.21, 16.32) * mm, "end": v(-31.34, 15.93) * mm});
            skLineSegment(sketch, "E168", {"start": v(-31.34, 15.93) * mm, "end": v(-31.48, 15.77) * mm});
            skLineSegment(sketch, "E169", {"start": v(-31.48, 15.77) * mm, "end": v(-31.83, 15.7) * mm});
            skLineSegment(sketch, "E170", {"start": v(-31.83, 15.7) * mm, "end": v(-32.44, 15.78) * mm});
            skLineSegment(sketch, "E171", {"start": v(-32.44, 15.78) * mm, "end": v(-32.95, 15.81) * mm});
            skLineSegment(sketch, "E172", {"start": v(-32.95, 15.81) * mm, "end": v(-33.12, 15.78) * mm});
            skLineSegment(sketch, "E173", {"start": v(-33.12, 15.78) * mm, "end": v(-33.08, 15.63) * mm});
            skLineSegment(sketch, "E174", {"start": v(-33.08, 15.63) * mm, "end": v(-32.93, 15.5) * mm});
            skLineSegment(sketch, "E175", {"start": v(-32.93, 15.5) * mm, "end": v(-32.15, 14.9) * mm});
            skLineSegment(sketch, "E176", {"start": v(-32.15, 14.9) * mm, "end": v(-31.61, 14.42) * mm});
            skLineSegment(sketch, "E177", {"start": v(-31.61, 14.42) * mm, "end": v(-31.43, 14.24) * mm});
            skLineSegment(sketch, "E178", {"start": v(-31.43, 14.24) * mm, "end": v(-31.22, 14.25) * mm});
            skLineSegment(sketch, "E179", {"start": v(-31.22, 14.25) * mm, "end": v(-30.98, 14.4) * mm});
            skLineSegment(sketch, "E180", {"start": v(-30.98, 14.4) * mm, "end": v(-30.73, 14.74) * mm});
            skLineSegment(sketch, "E181", {"start": v(-30.73, 14.74) * mm, "end": v(-30.53, 15.34) * mm});
            skLineSegment(sketch, "E182", {"start": v(-30.53, 15.34) * mm, "end": v(-30.37, 16.09) * mm});
            skLineSegment(sketch, "E183", {"start": v(-30.37, 16.09) * mm, "end": v(-30.31, 17.1) * mm});
            skLineSegment(sketch, "E184", {"start": v(-30.31, 17.1) * mm, "end": v(-30.38, 17.9) * mm});
            skLineSegment(sketch, "E185", {"start": v(-30.38, 17.9) * mm, "end": v(-30.46, 18.17) * mm});
            skLineSegment(sketch, "E186", {"start": v(-30.16, 22.1) * mm, "end": v(-30.4, 22.15) * mm});
            skLineSegment(sketch, "E187", {"start": v(-30.4, 22.15) * mm, "end": v(-30.73, 22.12) * mm});
            skLineSegment(sketch, "E188", {"start": v(-30.73, 22.12) * mm, "end": v(-31.26, 22) * mm});
            skLineSegment(sketch, "E189", {"start": v(-31.26, 22) * mm, "end": v(-31.76, 21.9) * mm});
            skLineSegment(sketch, "E190", {"start": v(-31.76, 21.9) * mm, "end": v(-31.71, 22.75) * mm});
            skLineSegment(sketch, "E191", {"start": v(-31.71, 22.75) * mm, "end": v(-31.68, 23.07) * mm});
            skLineSegment(sketch, "E192", {"start": v(-31.68, 23.07) * mm, "end": v(-31.82, 23.16) * mm});
            skLineSegment(sketch, "E193", {"start": v(-31.82, 23.16) * mm, "end": v(-31.91, 23.29) * mm});
            skLineSegment(sketch, "E194", {"start": v(-31.91, 23.29) * mm, "end": v(-31.03, 23.43) * mm});
            skLineSegment(sketch, "E195", {"start": v(-31.03, 23.43) * mm, "end": v(-30.33, 23.5) * mm});
            skLineSegment(sketch, "E196", {"start": v(-30.33, 23.5) * mm, "end": v(-29.83, 23.52) * mm});
            skLineSegment(sketch, "E197", {"start": v(-29.83, 23.52) * mm, "end": v(-29.53, 23.45) * mm});
            skLineSegment(sketch, "E198", {"start": v(-29.53, 23.45) * mm, "end": v(-29.5, 23.33) * mm});
            skLineSegment(sketch, "E199", {"start": v(-29.5, 23.33) * mm, "end": v(-29.53, 23.14) * mm});
            skLineSegment(sketch, "E200", {"start": v(-29.53, 23.14) * mm, "end": v(-29.78, 22.4) * mm});
            skLineSegment(sketch, "E201", {"start": v(-29.78, 22.4) * mm, "end": v(-29.93, 22.05) * mm});
            skLineSegment(sketch, "E202", {"start": v(-29.93, 22.05) * mm, "end": v(-29.98, 21.95) * mm});
            skLineSegment(sketch, "E203", {"start": v(-29.98, 21.95) * mm, "end": v(-30.1, 22) * mm});
            skLineSegment(sketch, "E204", {"start": v(-30.1, 22) * mm, "end": v(-30.16, 22.1) * mm});
            skLineSegment(sketch, "E205", {"start": v(-34.1, 21.54) * mm, "end": v(-34.28, 22.08) * mm});
            skLineSegment(sketch, "E206", {"start": v(-34.28, 22.08) * mm, "end": v(-34.4, 22.8) * mm});
            skLineSegment(sketch, "E207", {"start": v(-34.4, 22.8) * mm, "end": v(-33.56, 23) * mm});
            skLineSegment(sketch, "E208", {"start": v(-33.56, 23) * mm, "end": v(-32.43, 23.2) * mm});
            skLineSegment(sketch, "E209", {"start": v(-32.43, 23.2) * mm, "end": v(-32.43, 23.09) * mm});
            skLineSegment(sketch, "E210", {"start": v(-32.43, 23.09) * mm, "end": v(-32.4, 22.82) * mm});
            skLineSegment(sketch, "E211", {"start": v(-32.4, 22.82) * mm, "end": v(-32.34, 22.4) * mm});
            skLineSegment(sketch, "E212", {"start": v(-32.34, 22.4) * mm, "end": v(-32.27, 21.8) * mm});
            skLineSegment(sketch, "E213", {"start": v(-32.27, 21.8) * mm, "end": v(-34.1, 21.54) * mm});
            skSolve(sketch);
        }
        {
            var Q0;
            Q0 = qSketchRegion(id + "F6", true);
            extrude(context, id + "F7", {"entities" : qUnion([Q0]), "operationType" : NewBodyOperationType.ADD, "depth" : 1 * mm});
        }
    });
